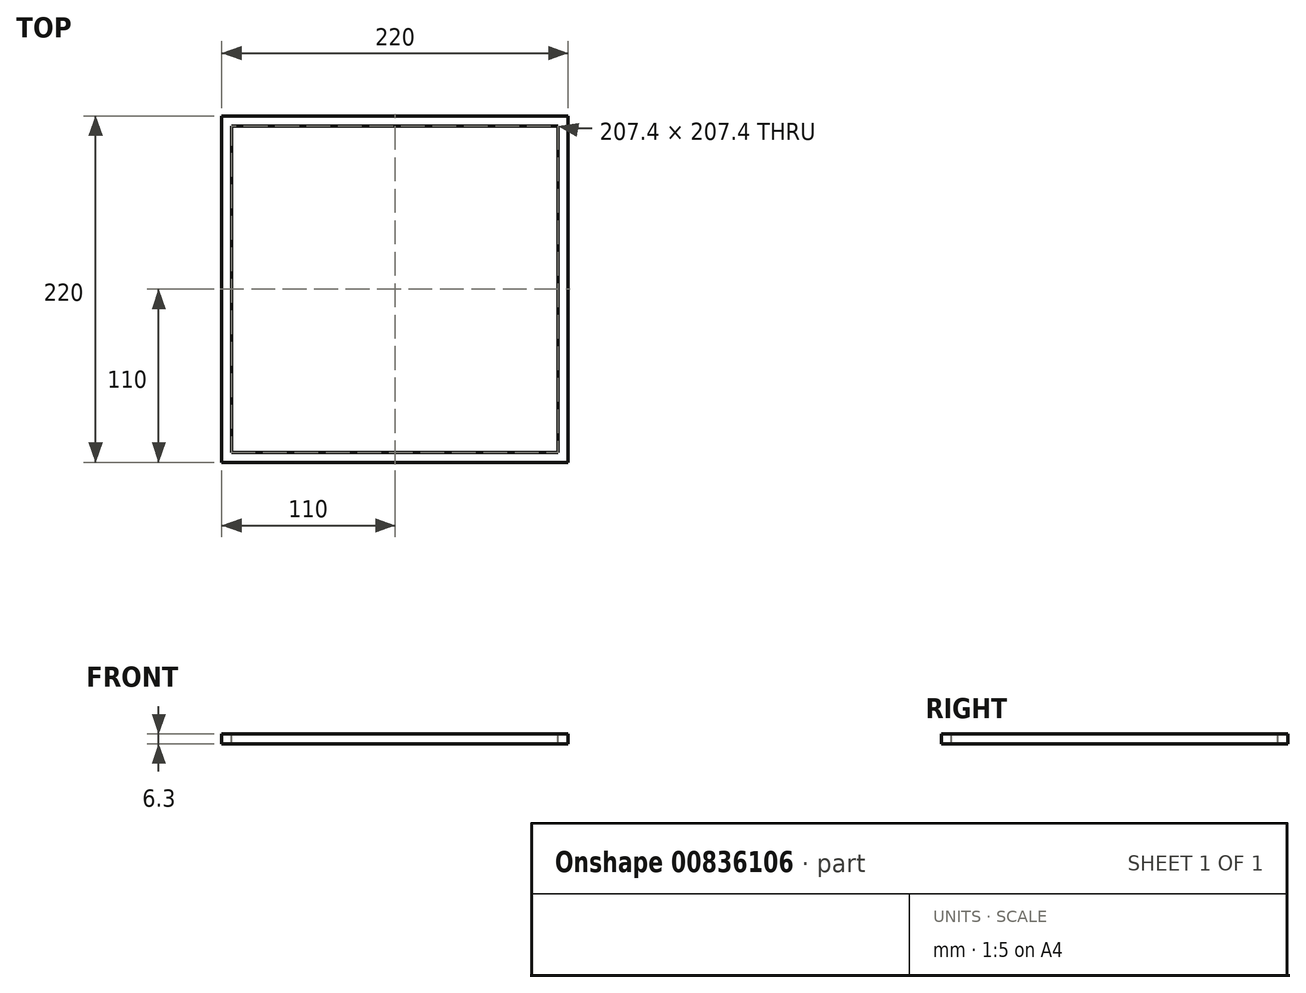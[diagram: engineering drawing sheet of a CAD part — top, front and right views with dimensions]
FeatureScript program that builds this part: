
annotation { "Feature Type Name" : "Feature", "Feature Type Description" : "" }
export const myFeature = defineFeature(function(context is Context, id is Id, definition is map)
    precondition{}
    {
        {
            var Q0;
            Q0=qCreatedBy(makeId("Top.planeOp"),FACE);
            var sketch = newSketch(context, id + "F0", { "sketchPlane" : qUnion([Q0])});
            skLineSegment(sketch, "E0.bottom", {"start": v(-110, 110) * mm, "end": v(110, 110) * mm});
            skLineSegment(sketch, "E0.top", {"start": v(-110, -110) * mm, "end": v(110, -110) * mm});
            skLineSegment(sketch, "E0.left", {"start": v(-110, 110) * mm, "end": v(-110, -110) * mm});
            skLineSegment(sketch, "E0.right", {"start": v(110, 110) * mm, "end": v(110, -110) * mm});
            skPoint(sketch, "E0.middle", {"position": v(0, 0) * mm});
            skSolve(sketch);
        }
        {
            var Q0;
            Q0 = qSketchRegion(id + "F0", true);
            extrude(context, id + "F1", {"entities" : qUnion([Q0]), "oppositeDirection" : true, "depth" : 6.3 * mm, "offsetDistance" : 25 * mm});
        }
        {
            var Q0;
            Q0=makeQuery(id+"F1.opExtrude","CAP_FACE",FACE,{"disambiguationData":[OSD([sQuery(id+"F0.wireOp",EDGE,"E0.bottom"),sQuery(id+"F0.wireOp",EDGE,"E0.top"),sQuery(id+"F0.wireOp",EDGE,"E0.left"),sQuery(id+"F0.wireOp",EDGE,"E0.right")])],"isStart":true});
            var sketch = newSketch(context, id + "F2", { "sketchPlane" : qUnion([Q0])});
            skLineSegment(sketch, "E1.bottom", {"start": v(-103.7, 103.7) * mm, "end": v(103.7, 103.7) * mm});
            skLineSegment(sketch, "E1.top", {"start": v(-103.7, -103.7) * mm, "end": v(103.7, -103.7) * mm});
            skLineSegment(sketch, "E1.left", {"start": v(-103.7, 103.7) * mm, "end": v(-103.7, -103.7) * mm});
            skLineSegment(sketch, "E1.right", {"start": v(103.7, 103.7) * mm, "end": v(103.7, -103.7) * mm});
            skPoint(sketch, "E1.middle", {"position": v(0, 0) * mm});
            skSolve(sketch);
        }
        {
            var Q0;
            Q0=makeQuery(id+"F2.imprint","IMPRINT",FACE,{"disambiguationData":[TD([[makeQuery(id+"F2.imprint","IMPRINT",EDGE,{"derivedFrom":sQuery(id+"F2.wireOp",EDGE,"E1.bottom")}),-1.0]])]});
            extrude(context, id + "F3", {"entities" : qUnion([Q0]), "operationType" : NewBodyOperationType.REMOVE, "endBound" : BoundingType.THROUGH_ALL, "oppositeDirection" : true, "depth" : 25 * mm, "offsetDistance" : 25 * mm});
        }
    });
